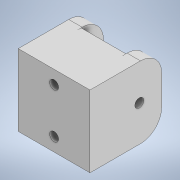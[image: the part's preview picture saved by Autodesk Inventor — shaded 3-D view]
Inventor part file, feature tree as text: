
AUTODESK INVENTOR PART (.ipt)
format: ipt  version: 2022 (Build 260153000, 153)  size: 160,256 bytes
history: native  units: mm
features: sketch x6, extrude x5, plane x1, revolve x1, fillet x1
ambient origin geometry x8: Origin, YZ Plane, XZ Plane, XY Plane, X Axis, Y Axis, Z Axis, Center Point
bodies: Solid1 (feature_tree)
feature tree (14):
  extrude  "Extrusion1"  Depth=20.0mm
  plane  "Work Plane1"
  revolve  "Revolution1"  [1 undecoded]
  fillet  "Fillet1"  Radius=5.0mm
  extrude  "Extrusion2"  Depth=4.75mm
  extrude  "Extrusion3"  Depth=2.0mm
  extrude  "Extrusion4"  Depth=2.0mm
  extrude  "Extrusion5"  Depth=10.0mm TaperAngle=0.0deg
  sketch  "Sketch1"  dims[d0=16.0mm d1=20.0mm]
  sketch  "Sketch2"  dims[d2=16.0mm d3=0.0mm d4=-5.0mm d5=5.0mm]
  sketch  "Sketch3"  dims[d7=90.0deg d8=4.75mm]
  sketch  "Sketch4"  dims[d9=4.0mm d10=0.0mm d12=2.0mm]
  sketch  "Sketch5"  dims[d13=4.0mm d14=0.0mm d16=2.0mm]
  sketch  "Sketch6"  dims[d18=10.0mm d19=0.0mm d20=10.0mm d21=0.0mm]
note: 1 required parameter value undecoded (feature->parameter linkage not recoverable at this tier; creation-order binding heuristic only, values carry confidence <= 0.55)
